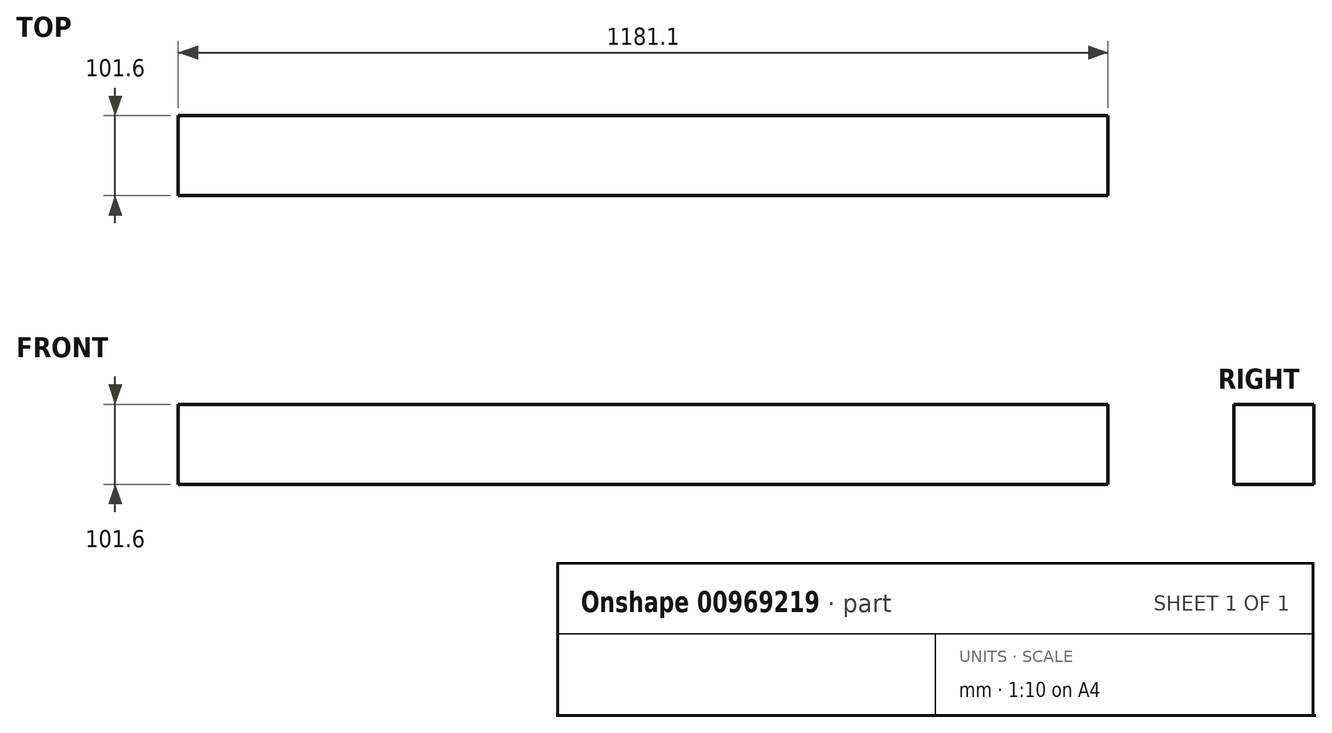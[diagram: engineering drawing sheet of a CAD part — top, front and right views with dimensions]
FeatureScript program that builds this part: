
annotation { "Feature Type Name" : "Feature", "Feature Type Description" : "" }
export const myFeature = defineFeature(function(context is Context, id is Id, definition is map)
    precondition{}
    {
        {
            var Q0;
            Q0=qCreatedBy(makeId("Right.planeOp"),FACE);
            var sketch = newSketch(context, id + "F0", { "sketchPlane" : qUnion([Q0])});
            skLineSegment(sketch, "E0.bottom", {"start": v(-50.8, -50.8) * mm, "end": v(50.8, -50.8) * mm});
            skLineSegment(sketch, "E0.top", {"start": v(-50.8, 50.8) * mm, "end": v(50.8, 50.8) * mm});
            skLineSegment(sketch, "E0.left", {"start": v(-50.8, -50.8) * mm, "end": v(-50.8, 50.8) * mm});
            skLineSegment(sketch, "E0.right", {"start": v(50.8, -50.8) * mm, "end": v(50.8, 50.8) * mm});
            skPoint(sketch, "E0.middle", {"position": v(0, 0) * mm});
            skSolve(sketch);
        }
        {
            var Q0;
            Q0 = qSketchRegion(id + "F0", true);
            extrude(context, id + "F1", {"entities" : qUnion([Q0]), "endBound" : BoundingType.SYMMETRIC, "oppositeDirection" : true, "depth" : 1181.1 * mm, "offsetDistance" : 25.4 * mm});
        }
    });
